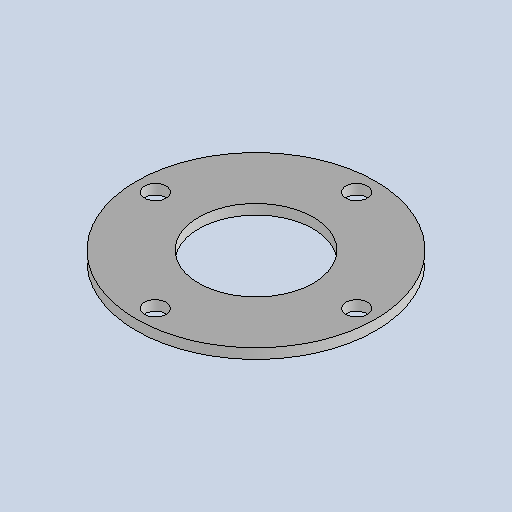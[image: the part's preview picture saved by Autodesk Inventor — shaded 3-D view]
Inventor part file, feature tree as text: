
AUTODESK INVENTOR PART (.ipt)
format: ipt  version: 2025.1 (Build 291241020, 241B)  size: 146,944 bytes
history: native  units: mm
features: other x3, sketch x2, sheet_metal_op x1, pattern_circular x1
ambient origin geometry x8: Origin, YZ Plane, XZ Plane, XY Plane, X Axis, Y Axis, Z Axis, Center Point
bodies: Body1 (feature_tree)
feature tree (7):
  sheet_metal_op  "Face2"
  pattern_circular  "Circular Pattern1"  [2 undecoded]
  sketch  "Sketch2"  dims[d14=8.0mm]
  other  "Plate2"
  sketch  "Sketch3"  dims[d15=17.0mm d17=8.0mm d18=0.0mm d19=40.0mm d20=360.0deg d25=91.0mm d27=190.0mm d28=160.0mm]
  other  "Cut1"
  other  "Definition1"
note: 2 required parameter values undecoded (feature->parameter linkage not recoverable at this tier; creation-order binding heuristic only, values carry confidence <= 0.55)
